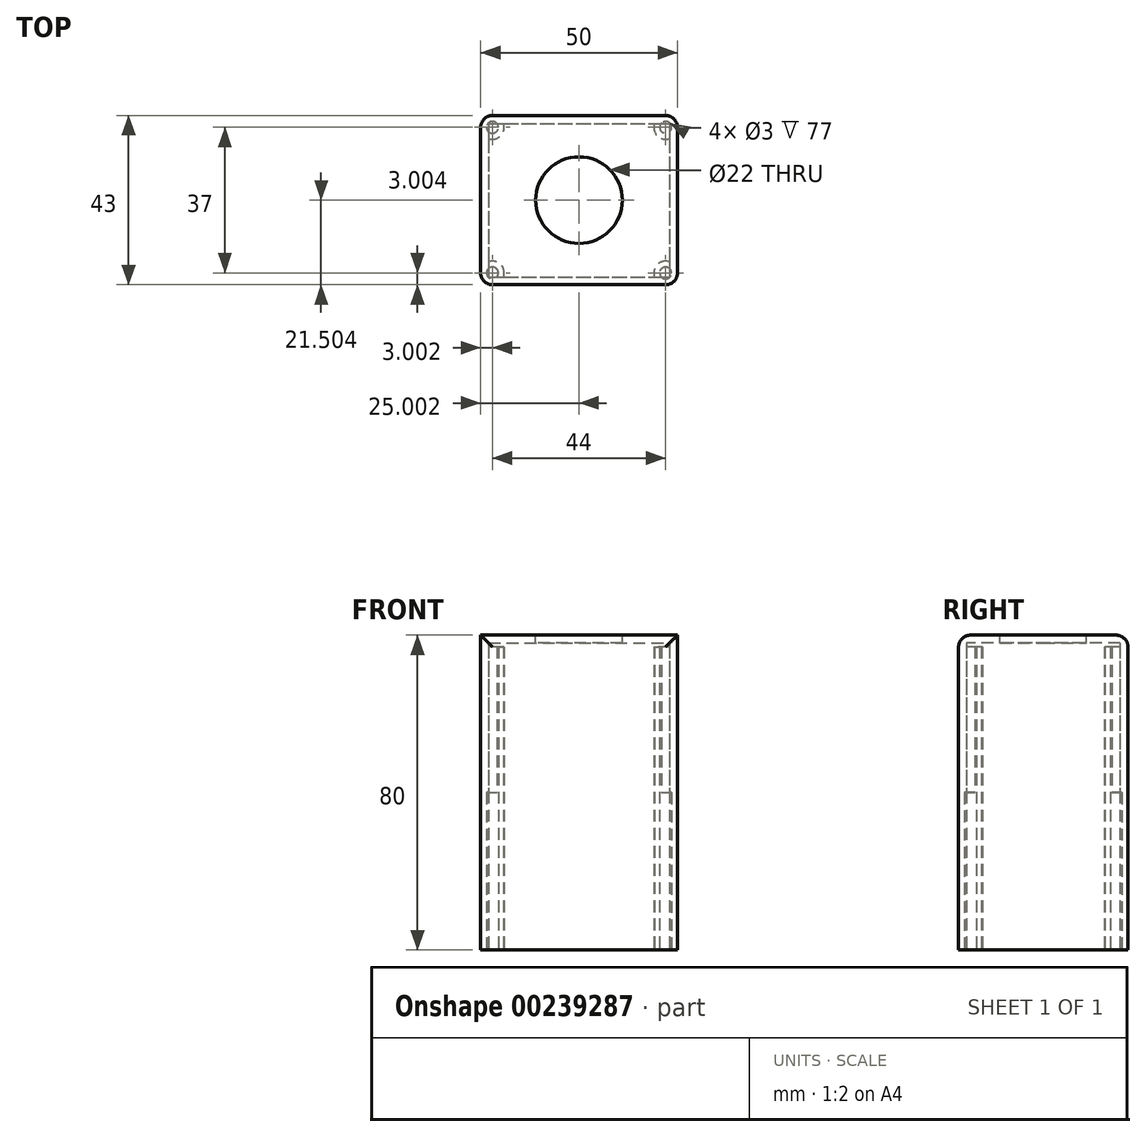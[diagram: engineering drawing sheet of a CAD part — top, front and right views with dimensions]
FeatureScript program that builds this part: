
annotation { "Feature Type Name" : "Feature", "Feature Type Description" : "" }
export const myFeature = defineFeature(function(context is Context, id is Id, definition is map)
    precondition{}
    {
        {
            var Q0;
            Q0=qCreatedBy(makeId("Top.planeOp"),FACE);
            var sketch = newSketch(context, id + "F0", { "sketchPlane" : qUnion([Q0])});
            skLineSegment(sketch, "E0.bottom", {"start": v(-34.03, 26.22) * mm, "end": v(15.97, 26.22) * mm});
            skLineSegment(sketch, "E0.top", {"start": v(-34.03, -16.78) * mm, "end": v(15.97, -16.78) * mm});
            skLineSegment(sketch, "E0.left", {"start": v(-34.03, 26.22) * mm, "end": v(-34.03, -16.78) * mm});
            skLineSegment(sketch, "E0.right", {"start": v(15.97, 26.22) * mm, "end": v(15.97, -16.78) * mm});
            skPoint(sketch, "E1", {"position": v(-31.03, -13.78) * mm});
            skPoint(sketch, "E2", {"position": v(-31.03, 23.22) * mm});
            skPoint(sketch, "E3", {"position": v(12.97, 23.22) * mm});
            skPoint(sketch, "E4", {"position": v(12.97, -13.78) * mm});
            skCircle(sketch, "E5", {"center": v(-31.03, 23.22) * mm, "radius": 1.5 * mm});
            skCircle(sketch, "E6", {"center": v(12.97, 23.22) * mm, "radius": 1.5 * mm});
            skCircle(sketch, "E7", {"center": v(-31.03, -13.78) * mm, "radius": 1.5 * mm});
            skCircle(sketch, "E8", {"center": v(12.97, -13.78) * mm, "radius": 1.5 * mm});
            skSolve(sketch);
        }
        {
            var Q0;
            Q0=makeQuery(id+"F0.imprint","IMPRINT",FACE,{"disambiguationData":[TD([[makeQuery(id+"F0.imprint","IMPRINT",EDGE,{"derivedFrom":sQuery(id+"F0.wireOp",EDGE,"E8")}),-1.0]])]});
            var Q1;
            Q1=makeQuery(id+"F0.imprint","IMPRINT",FACE,{"disambiguationData":[TD([[makeQuery(id+"F0.imprint","IMPRINT",EDGE,{"derivedFrom":sQuery(id+"F0.wireOp",EDGE,"E7")}),-1.0]])]});
            var Q2;
            Q2=makeQuery(id+"F0.imprint","IMPRINT",FACE,{"disambiguationData":[TD([[makeQuery(id+"F0.imprint","IMPRINT",EDGE,{"derivedFrom":sQuery(id+"F0.wireOp",EDGE,"E5")}),-1.0]])]});
            var Q3;
            Q3=makeQuery(id+"F0.imprint","IMPRINT",FACE,{"disambiguationData":[TD([[makeQuery(id+"F0.imprint","IMPRINT",EDGE,{"derivedFrom":sQuery(id+"F0.wireOp",EDGE,"E6")}),-1.0]])]});
            var Q4;
            {var subQ5=sQuery(id+"F0.wireOp",EDGE,"5a7f028d-dde4-426a-927e-fdb31705949f");var subQ13=sQuery(id+"F0.wireOp",EDGE,"E0.bottom");var subQ14=makeQuery(id+"F0.imprint","INTERSECT",VERTEX,{"derivedFrom":[subQ13,subQ5]});Q4=makeQuery(id+"F0.imprint","IMPRINT",FACE,{"disambiguationData":[TD([[makeQuery(id+"F0.imprint","IMPRINT",EDGE,{"disambiguationData":[TD([[subQ14,-1.0]])],"derivedFrom":subQ13}),-1.0]])]});}
            var Q5;
            Q5=makeQuery(id+"F0.imprint","IMPRINT",FACE,{"disambiguationData":[TD([[makeQuery(id+"F0.imprint","IMPRINT",EDGE,{"derivedFrom":sQuery(id+"F0.wireOp",EDGE,"E6")}),1.0]])]});
            var Q6;
            Q6=makeQuery(id+"F0.imprint","IMPRINT",FACE,{"disambiguationData":[TD([[makeQuery(id+"F0.imprint","IMPRINT",EDGE,{"derivedFrom":sQuery(id+"F0.wireOp",EDGE,"E8")}),1.0]])]});
            var Q7;
            Q7=makeQuery(id+"F0.imprint","IMPRINT",FACE,{"disambiguationData":[TD([[makeQuery(id+"F0.imprint","IMPRINT",EDGE,{"derivedFrom":sQuery(id+"F0.wireOp",EDGE,"E7")}),1.0]])]});
            var Q8;
            Q8=makeQuery(id+"F0.imprint","IMPRINT",FACE,{"disambiguationData":[TD([[makeQuery(id+"F0.imprint","IMPRINT",EDGE,{"derivedFrom":sQuery(id+"F0.wireOp",EDGE,"E5")}),1.0]])]});
            extrude(context, id + "F1", {"entities" : qUnion([Q0, Q1, Q2, Q3, Q4, Q5, Q6, Q7, Q8]), "depth" : 80 * mm});
        }
        {
            var Q0;
            Q0=makeQuery(id+"F1.opExtrude","CAP_FACE",FACE,{"disambiguationData":[OSD([sQuery(id+"F0.wireOp",EDGE,"E0.bottom"),sQuery(id+"F0.wireOp",EDGE,"E0.top"),sQuery(id+"F0.wireOp",EDGE,"E0.left"),sQuery(id+"F0.wireOp",EDGE,"E0.right")])],"isStart":false});
            var sketch = newSketch(context, id + "F2", { "sketchPlane" : qUnion([Q0])});
            skCircle(sketch, "E9", {"center": v(-9.03, 4.72) * mm, "radius": 11 * mm});
            skSolve(sketch);
        }
        {
            var Q0;
            Q0=makeQuery(id+"F1.opExtrude","CAP_FACE",FACE,{"disambiguationData":[OSD([sQuery(id+"F0.wireOp",EDGE,"E0.bottom"),sQuery(id+"F0.wireOp",EDGE,"E0.top"),sQuery(id+"F0.wireOp",EDGE,"E0.left"),sQuery(id+"F0.wireOp",EDGE,"E0.right")])],"isStart":true});
            shell(context, id + "F3", {"entities" : qUnion([Q0]), "thickness" : 2 * mm});
        }
        {
            var Q0;
            Q0=makeQuery(id+"F2.imprint","IMPRINT",FACE,{"disambiguationData":[TD([[makeQuery(id+"F2.imprint","IMPRINT",EDGE,{"derivedFrom":sQuery(id+"F2.wireOp",EDGE,"E9")}),1.0]])]});
            extrude(context, id + "F4", {"entities" : qUnion([Q0]), "operationType" : NewBodyOperationType.REMOVE, "oppositeDirection" : true, "depth" : 3.1 * mm});
        }
        {
            var Q0;
            Q0=makeQuery(id+"F1.opExtrude","SWEPT_EDGE",EDGE,{"disambiguationData":[OSD([sQuery(id+"F0.wireOp",EDGE,"E0.bottom"),sQuery(id+"F0.wireOp",EDGE,"E0.right")])]});
            var Q1;
            Q1=makeQuery(id+"F1.opExtrude","CAP_EDGE",EDGE,{"disambiguationData":[OSD([sQuery(id+"F0.wireOp",EDGE,"E0.bottom")])],"isStart":false});
            var Q2;
            Q2=makeQuery(id+"F1.opExtrude","SWEPT_EDGE",EDGE,{"disambiguationData":[OSD([sQuery(id+"F0.wireOp",EDGE,"E0.bottom"),sQuery(id+"F0.wireOp",EDGE,"E0.left")])]});
            var Q3;
            Q3=makeQuery(id+"F1.opExtrude","SWEPT_EDGE",EDGE,{"disambiguationData":[OSD([sQuery(id+"F0.wireOp",EDGE,"E0.top"),sQuery(id+"F0.wireOp",EDGE,"E0.right")])]});
            var Q4;
            Q4=makeQuery(id+"F1.opExtrude","CAP_EDGE",EDGE,{"disambiguationData":[OSD([sQuery(id+"F0.wireOp",EDGE,"E0.top")])],"isStart":false});
            var Q5;
            Q5=makeQuery(id+"F1.opExtrude","SWEPT_EDGE",EDGE,{"disambiguationData":[OSD([sQuery(id+"F0.wireOp",EDGE,"E0.top"),sQuery(id+"F0.wireOp",EDGE,"E0.left")])]});
            fillet(context, id + "F5", {"entities" : qUnion([Q0, Q1, Q2, Q3, Q4, Q5]), "radius" : 3 * mm, "tangentPropagation" : true, "allowEdgeOverflow" : false});
        }
        {
            var Q0;
            Q0=makeQuery(id+"F0.imprint","IMPRINT",FACE,{"disambiguationData":[TD([[makeQuery(id+"F0.imprint","IMPRINT",EDGE,{"derivedFrom":sQuery(id+"F0.wireOp",EDGE,"E0.bottom")}),-1.0]])]});
            var sketch = newSketch(context, id + "F6", { "sketchPlane" : qUnion([Q0])});
            skCircle(sketch, "E10", {"center": v(12.97, -13.78) * mm, "radius": 3 * mm});
            skCircle(sketch, "E11", {"center": v(12.97, 23.22) * mm, "radius": 3 * mm});
            skCircle(sketch, "E12", {"center": v(-31.03, -13.78) * mm, "radius": 3 * mm});
            skCircle(sketch, "E13", {"center": v(-31.03, 23.22) * mm, "radius": 3 * mm});
            skSolve(sketch);
        }
        {
            var Q0;
            Q0=makeQuery(id+"F6.imprint","IMPRINT",FACE,{"disambiguationData":[TD([[makeQuery(id+"F6.imprint","IMPRINT",EDGE,{"derivedFrom":makeQuery(id+"F0.imprint","IMPRINT",EDGE,{"derivedFrom":sQuery(id+"F0.wireOp",EDGE,"E8")})}),-1.0]])]});
            var Q1;
            Q1=makeQuery(id+"F6.imprint","IMPRINT",FACE,{"disambiguationData":[TD([[makeQuery(id+"F6.imprint","IMPRINT",EDGE,{"derivedFrom":makeQuery(id+"F0.imprint","IMPRINT",EDGE,{"derivedFrom":sQuery(id+"F0.wireOp",EDGE,"E6")})}),-1.0]])]});
            var Q2;
            Q2=makeQuery(id+"F6.imprint","IMPRINT",FACE,{"disambiguationData":[TD([[makeQuery(id+"F6.imprint","IMPRINT",EDGE,{"derivedFrom":makeQuery(id+"F0.imprint","IMPRINT",EDGE,{"derivedFrom":sQuery(id+"F0.wireOp",EDGE,"E7")})}),-1.0]])]});
            var Q3;
            Q3=makeQuery(id+"F6.imprint","IMPRINT",FACE,{"disambiguationData":[TD([[makeQuery(id+"F6.imprint","IMPRINT",EDGE,{"derivedFrom":makeQuery(id+"F0.imprint","IMPRINT",EDGE,{"derivedFrom":sQuery(id+"F0.wireOp",EDGE,"E5")})}),-1.0]])]});
            extrude(context, id + "F7", {"entities" : qUnion([Q0, Q1, Q2, Q3]), "operationType" : NewBodyOperationType.ADD, "depth" : 77 * mm});
        }
        {
            var Q0;
            Q0=makeQuery(id+"F0.imprint","IMPRINT",FACE,{"disambiguationData":[TD([[makeQuery(id+"F0.imprint","IMPRINT",EDGE,{"derivedFrom":sQuery(id+"F0.wireOp",EDGE,"E5")}),1.0]])]});
            var Q1;
            Q1=makeQuery(id+"F0.imprint","IMPRINT",FACE,{"disambiguationData":[TD([[makeQuery(id+"F0.imprint","IMPRINT",EDGE,{"derivedFrom":sQuery(id+"F0.wireOp",EDGE,"E6")}),1.0]])]});
            var Q2;
            Q2=makeQuery(id+"F0.imprint","IMPRINT",FACE,{"disambiguationData":[TD([[makeQuery(id+"F0.imprint","IMPRINT",EDGE,{"derivedFrom":sQuery(id+"F0.wireOp",EDGE,"E7")}),1.0]])]});
            var Q3;
            Q3=makeQuery(id+"F0.imprint","IMPRINT",FACE,{"disambiguationData":[TD([[makeQuery(id+"F0.imprint","IMPRINT",EDGE,{"derivedFrom":sQuery(id+"F0.wireOp",EDGE,"E8")}),1.0]])]});
            extrude(context, id + "F8", {"entities" : qUnion([Q0, Q1, Q2, Q3]), "operationType" : NewBodyOperationType.REMOVE, "depth" : 40 * mm});
        }
    });
